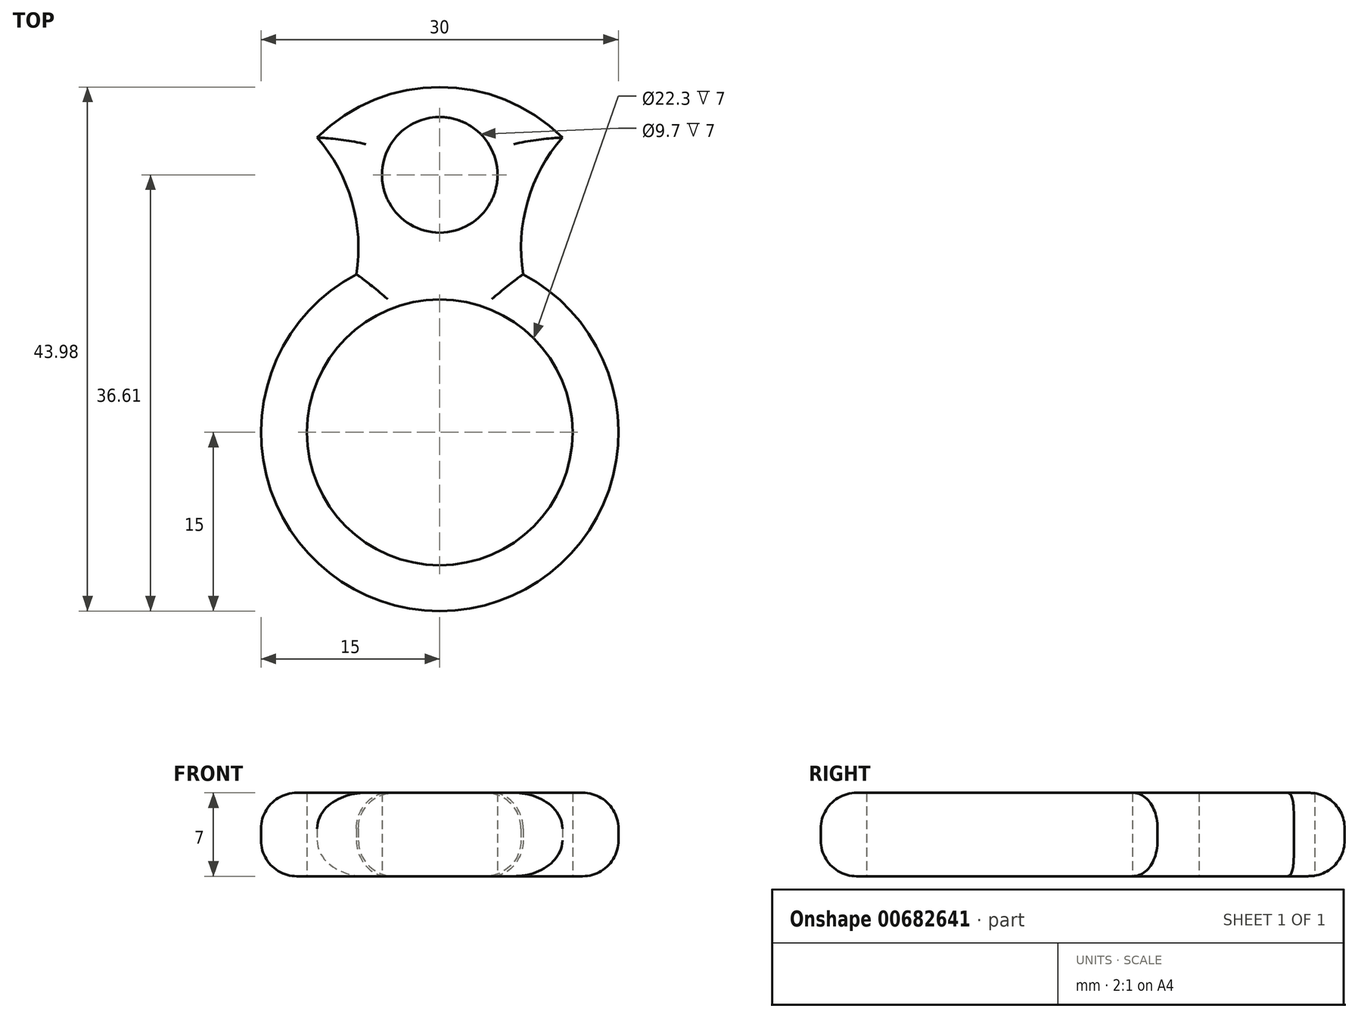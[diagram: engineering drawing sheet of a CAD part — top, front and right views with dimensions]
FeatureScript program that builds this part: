
annotation { "Feature Type Name" : "Feature", "Feature Type Description" : "" }
export const myFeature = defineFeature(function(context is Context, id is Id, definition is map)
    precondition{}
    {
        {
            var Q0;
            Q0=qCreatedBy(makeId("Top.planeOp"),FACE);
            var sketch = newSketch(context, id + "F0", { "sketchPlane" : qUnion([Q0])});
            skCircle(sketch, "E0", {"center": v(0, 0) * mm, "radius": 11.15 * mm});
            skCircle(sketch, "E1", {"center": v(0, 0) * mm, "radius": 15 * mm});
            skCircle(sketch, "E2", {"center": v(0, 21.61) * mm, "radius": 4.85 * mm});
            skArc(sketch, "E3", {"start": v(-7, 13.27) * mm, "mid": v(-7.37, 19.37) * mm, "end": v(-10.3, 24.74) * mm});
            skArc(sketch, "E4.MirrorCS", {"start": v(7, 13.27) * mm, "mid": v(7.37, 19.37) * mm, "end": v(10.3, 24.74) * mm});
            skArc(sketch, "E5", {"start": v(10.3, 24.74) * mm, "mid": v(0, 28.98) * mm, "end": v(-10.3, 24.74) * mm});
            skArc(sketch, "E6.1.0", {"start": v(-14.95, -0.5) * mm, "mid": v(-20.42, -3.23) * mm, "end": v(-26.52, -3.38) * mm});
            skArc(sketch, "E6.1.1", {"start": v(-26.52, -3.38) * mm, "mid": v(-25.05, -14.41) * mm, "end": v(-16.23, -21.2) * mm});
            skArc(sketch, "E6.1.2", {"start": v(-7.95, -12.62) * mm, "mid": v(-13.04, -16) * mm, "end": v(-16.23, -21.2) * mm});
            skCircle(sketch, "E6.1.3", {"center": v(-18.67, -10.73) * mm, "radius": 4.85 * mm});
            skArc(sketch, "E6.2.0", {"start": v(7.95, -12.62) * mm, "mid": v(13.04, -16) * mm, "end": v(16.23, -21.2) * mm});
            skArc(sketch, "E6.2.1", {"start": v(16.23, -21.2) * mm, "mid": v(25.05, -14.41) * mm, "end": v(26.52, -3.38) * mm});
            skArc(sketch, "E6.2.2", {"start": v(14.95, -0.5) * mm, "mid": v(20.42, -3.23) * mm, "end": v(26.52, -3.38) * mm});
            skCircle(sketch, "E6.2.3", {"center": v(18.67, -10.73) * mm, "radius": 4.85 * mm});
            skPoint(sketch, "E6.center", {"position": v(0, 0.05) * mm});
            skSolve(sketch);
        }
        {
            var Q0;
            {var subQ0=sQuery(id+"F0.wireOp",EDGE,"952e6613-98fb-4001-b2d4-6f389e16577f.1.0");Q0=makeQuery(id+"F0.imprint","IMPRINT",FACE,{"disambiguationData":[TD([[makeQuery(id+"F0.imprint","IMPRINT",EDGE,{"derivedFrom":subQ0}),1.0]])]});}
            var Q1;
            {var subQ0=sQuery(id+"F0.wireOp",EDGE,"eFOhyOlN-bna7-62Th-JtA1-QydvIXZMZCIB");Q1=makeQuery(id+"F0.imprint","IMPRINT",FACE,{"disambiguationData":[TD([[makeQuery(id+"F0.imprint","IMPRINT",EDGE,{"derivedFrom":subQ0}),-1.0]])]});}
            var Q2;
            {var subQ0=sQuery(id+"F0.wireOp",EDGE,"952e6613-98fb-4001-b2d4-6f389e16577f.2.0");Q2=makeQuery(id+"F0.imprint","IMPRINT",FACE,{"disambiguationData":[TD([[makeQuery(id+"F0.imprint","IMPRINT",EDGE,{"derivedFrom":subQ0}),1.0]])]});}
            var Q3;
            Q3=makeQuery(id+"F0.imprint","IMPRINT",FACE,{"disambiguationData":[TD([[makeQuery(id+"F0.imprint","IMPRINT",EDGE,{"derivedFrom":sQuery(id+"F0.wireOp",EDGE,"E0")}),-1.0]])]});
            var Q4;
            {var subQ0=sQuery(id+"F0.wireOp",EDGE,"E6.1.0");Q4=makeQuery(id+"F0.imprint","IMPRINT",FACE,{"disambiguationData":[TD([[makeQuery(id+"F0.imprint","IMPRINT",EDGE,{"derivedFrom":subQ0}),1.0]])]});}
            var Q5;
            {var subQ1=sQuery(id+"F0.wireOp",EDGE,"E6.2.0");Q5=makeQuery(id+"F0.imprint","IMPRINT",FACE,{"disambiguationData":[TD([[makeQuery(id+"F0.imprint","IMPRINT",EDGE,{"derivedFrom":subQ1}),1.0]])]});}
            var Q6;
            Q6=makeQuery(id+"F0.imprint","IMPRINT",FACE,{"disambiguationData":[TD([[makeQuery(id+"F0.imprint","IMPRINT",EDGE,{"derivedFrom":sQuery(id+"F0.wireOp",EDGE,"E2")}),-1.0]])]});
            extrude(context, id + "F1", {"entities" : qUnion([Q0, Q1, Q2, Q3, Q4, Q5, Q6]), "depth" : 7 * mm, "offsetDistance" : 25 * mm});
        }
        {
            var Q0;
            Q0=makeQuery(id+"F1.opExtrude","CAP_EDGE",EDGE,{"disambiguationData":[OSD([sQuery(id+"F0.wireOp",EDGE,"E6.1.2")])],"isStart":false});
            var Q1;
            Q1=makeQuery(id+"F1.opExtrude","CAP_EDGE",EDGE,{"disambiguationData":[OSD([sQuery(id+"F0.wireOp",EDGE,"E6.1.1")])],"isStart":false});
            var Q2;
            Q2=makeQuery(id+"F1.opExtrude","CAP_EDGE",EDGE,{"disambiguationData":[OSD([sQuery(id+"F0.wireOp",EDGE,"E6.1.0")])],"isStart":false});
            var Q3;
            {var subQ0=sQuery(id+"F0.wireOp",EDGE,"E1");Q3=makeQuery(id+"F1.opExtrude","CAP_EDGE",EDGE,{"disambiguationData":[OSD([subQ0]),TDD([makeQuery(id+"F0.imprint","IMPRINT",EDGE,{"disambiguationData":[TD([[makeQuery(id+"F0.imprint","INTERSECT",VERTEX,{"derivedFrom":[subQ0,sQuery(id+"F0.wireOp",EDGE,"E6.1.2")]}),-1.0]])],"derivedFrom":subQ0})])],"isStart":false});}
            var Q4;
            Q4=makeQuery(id+"F1.opExtrude","CAP_EDGE",EDGE,{"disambiguationData":[OSD([sQuery(id+"F0.wireOp",EDGE,"E6.2.0")])],"isStart":false});
            var Q5;
            Q5=makeQuery(id+"F1.opExtrude","CAP_EDGE",EDGE,{"disambiguationData":[OSD([sQuery(id+"F0.wireOp",EDGE,"E6.2.1")])],"isStart":false});
            var Q6;
            Q6=makeQuery(id+"F1.opExtrude","CAP_EDGE",EDGE,{"disambiguationData":[OSD([sQuery(id+"F0.wireOp",EDGE,"E6.2.2")])],"isStart":false});
            var Q7;
            {var subQ0=sQuery(id+"F0.wireOp",EDGE,"E1");Q7=makeQuery(id+"F1.opExtrude","CAP_EDGE",EDGE,{"disambiguationData":[OSD([subQ0]),TDD([makeQuery(id+"F0.imprint","IMPRINT",EDGE,{"disambiguationData":[TD([[makeQuery(id+"F0.imprint","INTERSECT",VERTEX,{"derivedFrom":[subQ0,sQuery(id+"F0.wireOp",EDGE,"E3")]}),-1.0]])],"derivedFrom":subQ0})])],"isStart":false});}
            var Q8;
            {var subQ0=sQuery(id+"F0.wireOp",EDGE,"E1");Q8=makeQuery(id+"F1.opExtrude","CAP_EDGE",EDGE,{"disambiguationData":[OSD([subQ0]),TDD([makeQuery(id+"F0.imprint","IMPRINT",EDGE,{"disambiguationData":[TD([[makeQuery(id+"F0.imprint","INTERSECT",VERTEX,{"derivedFrom":[subQ0,sQuery(id+"F0.wireOp",EDGE,"E4.MirrorCS")]}),1.0]])],"derivedFrom":subQ0})])],"isStart":false});}
            var Q9;
            Q9=makeQuery(id+"F1.opExtrude","CAP_EDGE",EDGE,{"disambiguationData":[OSD([sQuery(id+"F0.wireOp",EDGE,"E4.MirrorCS")])],"isStart":false});
            var Q10;
            Q10=makeQuery(id+"F1.opExtrude","CAP_EDGE",EDGE,{"disambiguationData":[OSD([sQuery(id+"F0.wireOp",EDGE,"E5")])],"isStart":false});
            var Q11;
            Q11=makeQuery(id+"F1.opExtrude","CAP_EDGE",EDGE,{"disambiguationData":[OSD([sQuery(id+"F0.wireOp",EDGE,"E3")])],"isStart":false});
            var Q12;
            Q12=makeQuery(id+"F1.opExtrude","CAP_EDGE",EDGE,{"disambiguationData":[OSD([sQuery(id+"F0.wireOp",EDGE,"E6.1.1")])],"isStart":true});
            var Q13;
            Q13=makeQuery(id+"F1.opExtrude","CAP_EDGE",EDGE,{"disambiguationData":[OSD([sQuery(id+"F0.wireOp",EDGE,"E6.1.2")])],"isStart":true});
            var Q14;
            Q14=makeQuery(id+"F1.opExtrude","CAP_EDGE",EDGE,{"disambiguationData":[OSD([sQuery(id+"F0.wireOp",EDGE,"E6.1.0")])],"isStart":true});
            var Q15;
            {var subQ0=sQuery(id+"F0.wireOp",EDGE,"E1");Q15=makeQuery(id+"F1.opExtrude","CAP_EDGE",EDGE,{"disambiguationData":[OSD([subQ0]),TDD([makeQuery(id+"F0.imprint","IMPRINT",EDGE,{"disambiguationData":[TD([[makeQuery(id+"F0.imprint","INTERSECT",VERTEX,{"derivedFrom":[subQ0,sQuery(id+"F0.wireOp",EDGE,"E3")]}),-1.0]])],"derivedFrom":subQ0})])],"isStart":true});}
            var Q16;
            Q16=makeQuery(id+"F1.opExtrude","CAP_EDGE",EDGE,{"disambiguationData":[OSD([sQuery(id+"F0.wireOp",EDGE,"E3")])],"isStart":true});
            var Q17;
            Q17=makeQuery(id+"F1.opExtrude","CAP_EDGE",EDGE,{"disambiguationData":[OSD([sQuery(id+"F0.wireOp",EDGE,"E5")])],"isStart":true});
            var Q18;
            Q18=makeQuery(id+"F1.opExtrude","CAP_EDGE",EDGE,{"disambiguationData":[OSD([sQuery(id+"F0.wireOp",EDGE,"E4.MirrorCS")])],"isStart":true});
            var Q19;
            {var subQ0=sQuery(id+"F0.wireOp",EDGE,"E1");Q19=makeQuery(id+"F1.opExtrude","CAP_EDGE",EDGE,{"disambiguationData":[OSD([subQ0]),TDD([makeQuery(id+"F0.imprint","IMPRINT",EDGE,{"disambiguationData":[TD([[makeQuery(id+"F0.imprint","INTERSECT",VERTEX,{"derivedFrom":[subQ0,sQuery(id+"F0.wireOp",EDGE,"E4.MirrorCS")]}),1.0]])],"derivedFrom":subQ0})])],"isStart":true});}
            var Q20;
            Q20=makeQuery(id+"F1.opExtrude","CAP_EDGE",EDGE,{"disambiguationData":[OSD([sQuery(id+"F0.wireOp",EDGE,"E6.2.2")])],"isStart":true});
            var Q21;
            Q21=makeQuery(id+"F1.opExtrude","CAP_EDGE",EDGE,{"disambiguationData":[OSD([sQuery(id+"F0.wireOp",EDGE,"E6.2.1")])],"isStart":true});
            var Q22;
            Q22=makeQuery(id+"F1.opExtrude","CAP_EDGE",EDGE,{"disambiguationData":[OSD([sQuery(id+"F0.wireOp",EDGE,"E6.2.0")])],"isStart":true});
            var Q23;
            {var subQ0=sQuery(id+"F0.wireOp",EDGE,"E1");Q23=makeQuery(id+"F1.opExtrude","CAP_EDGE",EDGE,{"disambiguationData":[OSD([subQ0]),TDD([makeQuery(id+"F0.imprint","IMPRINT",EDGE,{"disambiguationData":[TD([[makeQuery(id+"F0.imprint","INTERSECT",VERTEX,{"derivedFrom":[subQ0,sQuery(id+"F0.wireOp",EDGE,"E6.1.2")]}),-1.0]])],"derivedFrom":subQ0})])],"isStart":true});}
            fillet(context, id + "F2", {"entities" : qUnion([Q0, Q1, Q2, Q3, Q4, Q5, Q6, Q7, Q8, Q9, Q10, Q11, Q12, Q13, Q14, Q15, Q16, Q17, Q18, Q19, Q20, Q21, Q22, Q23]), "radius" : 3 * mm, "tangentPropagation" : true, "allowEdgeOverflow" : false});
        }
    });
